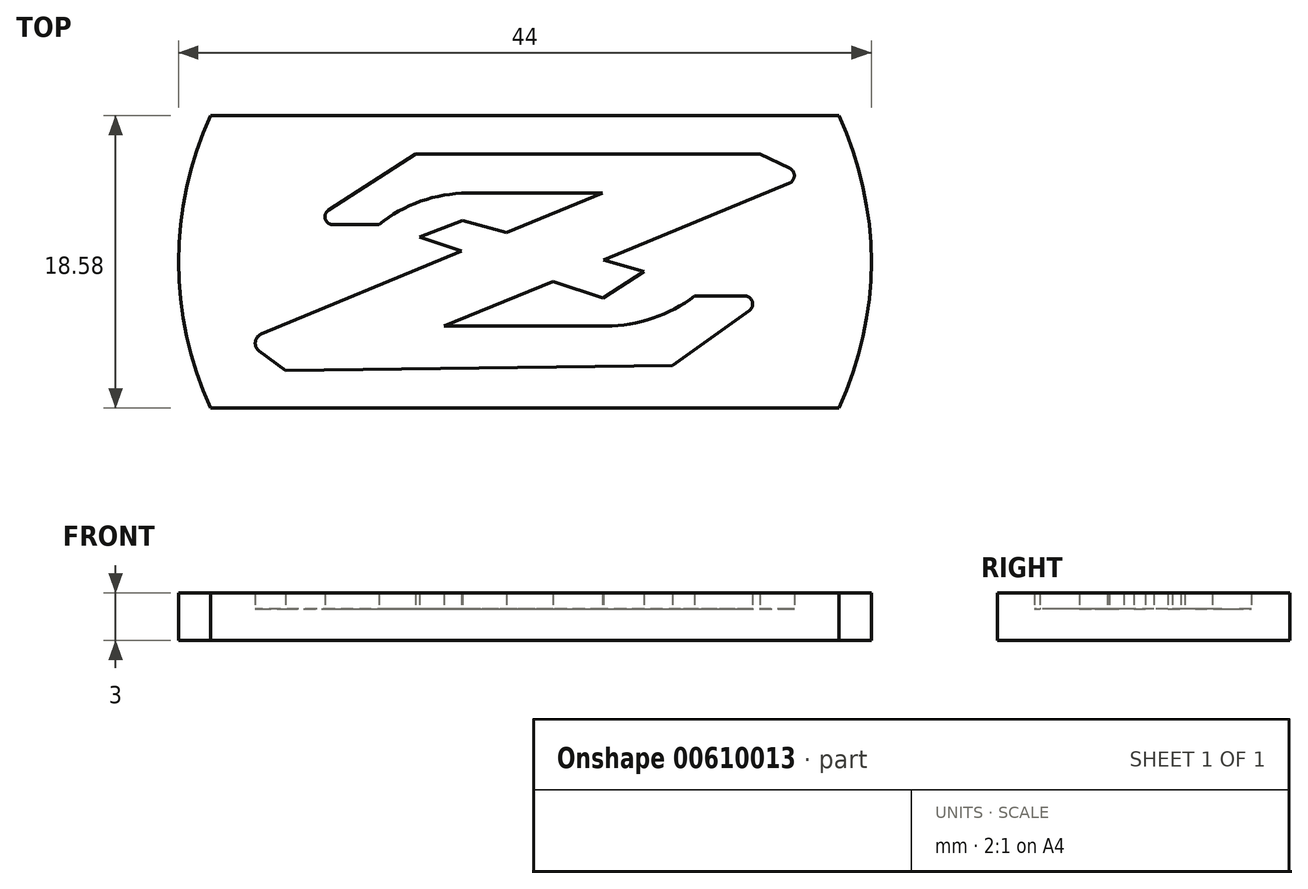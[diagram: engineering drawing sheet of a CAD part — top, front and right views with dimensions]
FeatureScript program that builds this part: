
annotation { "Feature Type Name" : "Feature", "Feature Type Description" : "" }
export const myFeature = defineFeature(function(context is Context, id is Id, definition is map)
    precondition{}
    {
        {
            var Q0;
            Q0=qCreatedBy(makeId("Top.planeOp"),FACE);
            var sketch = newSketch(context, id + "F0", { "sketchPlane" : qUnion([Q0])});
            skLineSegment(sketch, "E0", {"start": v(4.93, 4.36) * mm, "end": v(-3.62, 4.36) * mm});
            skLineSegment(sketch, "E1", {"start": v(-12.2, 2.36) * mm, "end": v(-9.28, 2.36) * mm});
            skArc(sketch, "E2", {"start": v(-3.62, 4.36) * mm, "mid": v(-6.62, 3.85) * mm, "end": v(-9.28, 2.36) * mm});
            skLineSegment(sketch, "E3", {"start": v(-12.47, 3.28) * mm, "end": v(-6.94, 6.85) * mm});
            skPoint(sketch, "E4.visualSharp", {"position": v(-13.9, 2.36) * mm});
            skArc(sketch, "E4.filletArc", {"start": v(-12.47, 3.28) * mm, "mid": v(-12.68, 2.72) * mm, "end": v(-12.2, 2.36) * mm});
            skLineSegment(sketch, "E5", {"start": v(14.94, 6.85) * mm, "end": v(16.82, 5.95) * mm});
            skLineSegment(sketch, "E6", {"start": v(-5.12, -4.07) * mm, "end": v(5.16, -4.07) * mm});
            skArc(sketch, "E7", {"start": v(5.16, -4.07) * mm, "mid": v(8.13, -3.58) * mm, "end": v(10.78, -2.17) * mm});
            skLineSegment(sketch, "E8", {"start": v(10.78, -2.17) * mm, "end": v(13.97, -2.17) * mm});
            skLineSegment(sketch, "E9", {"start": v(14.26, -3.08) * mm, "end": v(9.39, -6.57) * mm});
            skPoint(sketch, "E10.visualSharp", {"position": v(15.53, -2.17) * mm});
            skArc(sketch, "E10.filletArc", {"start": v(14.26, -3.08) * mm, "mid": v(14.45, -2.52) * mm, "end": v(13.97, -2.17) * mm});
            skLineSegment(sketch, "E11", {"start": v(-16.88, -5.66) * mm, "end": v(-15.2, -6.92) * mm});
            skLineSegment(sketch, "E12", {"start": v(-15.2, -6.92) * mm, "end": v(9.39, -6.57) * mm});
            skLineSegment(sketch, "E13", {"start": v(-6.67, 1.56) * mm, "end": v(-3.95, 2.64) * mm});
            skLineSegment(sketch, "E14", {"start": v(7.56, -0.62) * mm, "end": v(4.98, -2.3) * mm});
            skLineSegment(sketch, "E15", {"start": v(1.79, -1.25) * mm, "end": v(-5.12, -4.07) * mm});
            skPoint(sketch, "E16", {"position": v(-1.16, 1.85) * mm});
            skPoint(sketch, "E17", {"position": v(-4.01, 0.68) * mm});
            skPoint(sketch, "E18", {"position": v(4.98, 0.1) * mm});
            skLineSegment(sketch, "E19", {"start": v(-6.67, 1.56) * mm, "end": v(-4.01, 0.68) * mm});
            skLineSegment(sketch, "E20", {"start": v(-3.95, 2.64) * mm, "end": v(-1.16, 1.85) * mm});
            skLineSegment(sketch, "E21", {"start": v(4.93, 4.36) * mm, "end": v(-1.16, 1.85) * mm});
            skLineSegment(sketch, "E22", {"start": v(7.56, -0.62) * mm, "end": v(4.98, 0.1) * mm});
            skLineSegment(sketch, "E23", {"start": v(4.98, -2.3) * mm, "end": v(1.79, -1.25) * mm});
            skLineSegment(sketch, "E24", {"start": v(-4.01, 0.68) * mm, "end": v(-16.74, -4.6) * mm});
            skLineSegment(sketch, "E25", {"start": v(16.8, 5) * mm, "end": v(4.98, 0.1) * mm});
            skPoint(sketch, "E26.visualSharp", {"position": v(-17.74, -5) * mm});
            skArc(sketch, "E26.filletArc", {"start": v(-16.74, -4.6) * mm, "mid": v(-17.12, -5.09) * mm, "end": v(-16.88, -5.66) * mm});
            skPoint(sketch, "E27.visualSharp", {"position": v(17.88, 5.44) * mm});
            skArc(sketch, "E27.filletArc", {"start": v(16.8, 5) * mm, "mid": v(17.12, 5.46) * mm, "end": v(16.82, 5.95) * mm});
            skLineSegment(sketch, "E28", {"start": v(-6.94, 6.85) * mm, "end": v(14.94, 6.85) * mm});
            skPoint(sketch, "E29.middle", {"position": v(0, 0) * mm});
            skArc(sketch, "E30", {"start": v(-19.94, 9.29) * mm, "mid": v(-22, 0) * mm, "end": v(-19.94, -9.29) * mm});
            skLineSegment(sketch, "E31", {"start": v(-19.94, 9.29) * mm, "end": v(19.94, 9.29) * mm});
            skLineSegment(sketch, "E32", {"start": v(19.94, -9.29) * mm, "end": v(-19.94, -9.29) * mm});
            skArc(sketch, "E33.trimOffspring", {"start": v(19.94, -9.29) * mm, "mid": v(22, 0) * mm, "end": v(19.94, 9.29) * mm});
            skSolve(sketch);
        }
        {
            var Q0;
            Q0=makeQuery(id+"F0.imprint","IMPRINT",FACE,{"disambiguationData":[TD([[makeQuery(id+"F0.imprint","IMPRINT",EDGE,{"derivedFrom":sQuery(id+"F0.wireOp",EDGE,"E0")}),1.0]])]});
            extrude(context, id + "F1", {"entities" : qUnion([Q0]), "depth" : 3 * mm, "offsetDistance" : 25 * mm});
        }
        {
            var Q0;
            Q0=makeQuery(id+"F0.imprint","IMPRINT",FACE,{"disambiguationData":[TD([[makeQuery(id+"F0.imprint","IMPRINT",EDGE,{"derivedFrom":sQuery(id+"F0.wireOp",EDGE,"E0")}),-1.0]])]});
            extrude(context, id + "F2", {"entities" : qUnion([Q0]), "operationType" : NewBodyOperationType.ADD, "depth" : 2 * mm, "offsetDistance" : 25 * mm});
        }
    });
